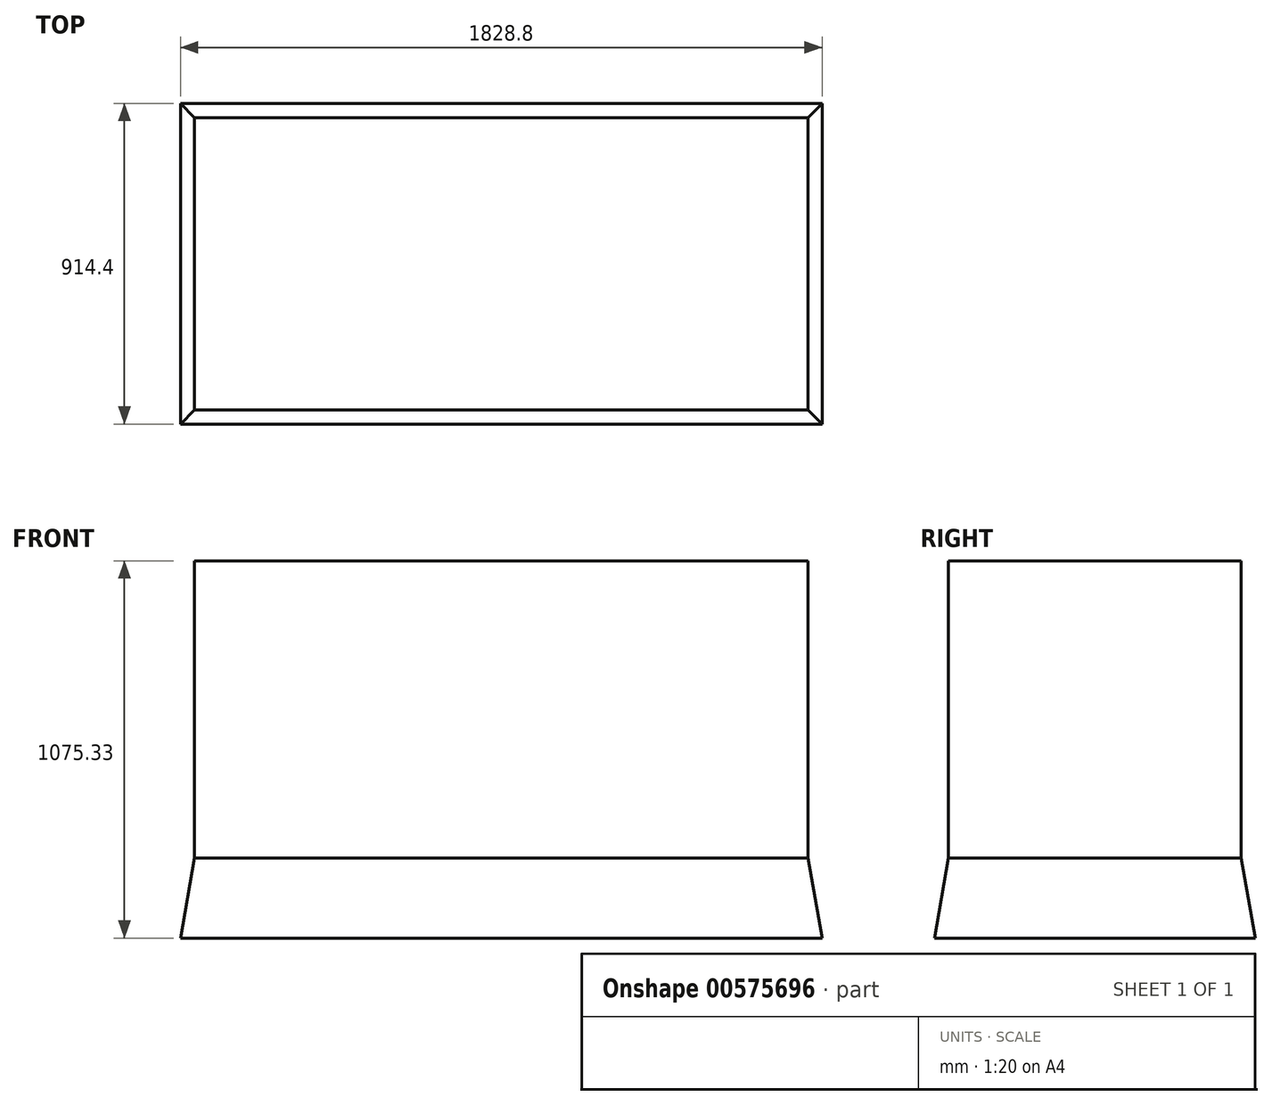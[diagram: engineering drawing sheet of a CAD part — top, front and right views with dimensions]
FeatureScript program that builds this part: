
annotation { "Feature Type Name" : "Feature", "Feature Type Description" : "" }
export const myFeature = defineFeature(function(context is Context, id is Id, definition is map)
    precondition{}
    {
        {
            var Q0;
            Q0=qCreatedBy(makeId("Top.planeOp"),FACE);
            var sketch = newSketch(context, id + "F0", { "sketchPlane" : qUnion([Q0])});
            skLineSegment(sketch, "E0.bottom", {"start": v(910.93, 457.2) * mm, "end": v(-917.87, 457.2) * mm});
            skLineSegment(sketch, "E0.top", {"start": v(910.93, -457.2) * mm, "end": v(-917.87, -457.2) * mm});
            skLineSegment(sketch, "E0.left", {"start": v(910.93, 457.2) * mm, "end": v(910.93, -457.2) * mm});
            skLineSegment(sketch, "E0.right", {"start": v(-917.87, 457.2) * mm, "end": v(-917.87, -457.2) * mm});
            skPoint(sketch, "E0.middle", {"position": v(-3.47, 0) * mm});
            skSolve(sketch);
        }
        {
            var Q0;
            Q0=makeQuery(id+"F0.imprint","IMPRINT",FACE,{"disambiguationData":[TD([[makeQuery(id+"F0.imprint","IMPRINT",EDGE,{"derivedFrom":sQuery(id+"F0.wireOp",EDGE,"E0.bottom")}),1.0]])]});
            extrude(context, id + "F1", {"entities" : qUnion([Q0]), "depth" : 0.25 * yard, "offsetDistance" : 0.03 * yard, "hasDraft" : true, "draftAngle" : 10 * degree, "draftPullDirection" : true});
        }
        {
            var Q0;
            Q0=makeQuery(id+"F1.opExtrude","CAP_FACE",FACE,{"disambiguationData":[OSD([sQuery(id+"F0.wireOp",EDGE,"E0.bottom"),sQuery(id+"F0.wireOp",EDGE,"E0.top"),sQuery(id+"F0.wireOp",EDGE,"E0.left"),sQuery(id+"F0.wireOp",EDGE,"E0.right")])],"isStart":false});
            extrude(context, id + "F2", {"entities" : qUnion([Q0]), "operationType" : NewBodyOperationType.ADD, "depth" : 0.27 * yard, "offsetDistance" : 0.03 * yard});
        }
        {
            var Q0;
            Q0=makeQuery(id+"F2.opExtrude","CAP_FACE",FACE,{"disambiguationData":[OSD([sQuery(id+"F0.wireOp",EDGE,"E0.bottom"),sQuery(id+"F0.wireOp",EDGE,"E0.top"),sQuery(id+"F0.wireOp",EDGE,"E0.left"),sQuery(id+"F0.wireOp",EDGE,"E0.right")])],"isStart":false});
            var Q1;
            Q1=makeQuery(id+"F2.opExtrude","CAP_FACE",FACE,{"disambiguationData":[OSD([sQuery(id+"F0.wireOp",EDGE,"E0.bottom"),sQuery(id+"F0.wireOp",EDGE,"E0.top"),sQuery(id+"F0.wireOp",EDGE,"E0.left"),sQuery(id+"F0.wireOp",EDGE,"E0.right")])],"isStart":false});
            extrude(context, id + "F3", {"entities" : qUnion([Q0, Q1]), "operationType" : NewBodyOperationType.ADD, "depth" : 0.34 * yard, "offsetDistance" : 0.03 * yard});
        }
        {
            var Q0;
            Q0=makeQuery(id+"F3.opExtrude","CAP_FACE",FACE,{"disambiguationData":[OSD([sQuery(id+"F0.wireOp",EDGE,"E0.bottom"),sQuery(id+"F0.wireOp",EDGE,"E0.top"),sQuery(id+"F0.wireOp",EDGE,"E0.left"),sQuery(id+"F0.wireOp",EDGE,"E0.right")])],"isStart":false});
            extrude(context, id + "F4", {"entities" : qUnion([Q0]), "operationType" : NewBodyOperationType.ADD, "depth" : 0.32 * yard, "offsetDistance" : 0.03 * yard});
        }
        {
            var Q0;
            Q0=makeQuery(id+"F4.opExtrude","CAP_FACE",FACE,{"disambiguationData":[OSD([sQuery(id+"F0.wireOp",EDGE,"E0.bottom"),sQuery(id+"F0.wireOp",EDGE,"E0.top"),sQuery(id+"F0.wireOp",EDGE,"E0.left"),sQuery(id+"F0.wireOp",EDGE,"E0.right")])],"isStart":false});
            extrude(context, id + "F5", {"entities" : qUnion([Q0]), "operationType" : NewBodyOperationType.ADD, "oppositeDirection" : true, "depth" : 0.4 * yard, "offsetDistance" : 0.03 * yard});
        }
    });
